# Revit family: Strangregulierventil für Differenzdruckmessung, Geradsitzform 4218 GMF
name_source: partatom
category: Rohrzubehör
units: mm (PartAtom-declared; Revit-internal decimal feet)

## family parameters
Arbeitsebenenbasiert = Nein
Beim Laden mit Abzugskörper schneiden = Nein
Bemaßung runder Anschluss = Durchmesser verwenden
Gemeinsam genutzt = Nein
Immer vertikal = Ja
OmniClass-Nummer = 23.65.55.14
OmniClass-Titel = Valves for Liquid Services
Teiletyp = Unterbricht

## types (1)
- Strangregulierventil für Differenzdruckmessung, Geradsitzform 4218 GMF
    Anwendungen = Zum hydraulischen Abgleich in Heiz- oder Kühlanlagen, Einregulieren und Absperren von Verteilleitungen, Strängen, Wärmetauschern, Heiz- und Kühlregistern.
    Ausführung = Geradsitzform, Gehäuse Grauguss GJL 250 nach EN 1561, Flansche nach EN 1092, PN 16; blau lackiert.
Messing Oberteil bis DN 100 geschraubt, ab DN 125 Ventiloberteil Grauguss mit nicht steigender Spindel, Spindelabdichtung durch Doppel-O-Ring.
Voreinstellung durch Hubbegrenzung mittels Innenspindel, digitale Anzeige der Voreinstellstufe im Handradfenster.
Zwei Schnellmessventile sind neben dem Handrad montiert.
    Differenzdruckmessnung = Das STRÖMAX-GMF Strangregulierventil ist mit zwei Schnellmessventilen ausgestattet:
Bei Verwendung eines geeigneten Messgerätes kann der Differenzdruck gemessen und dadurch die jeweilige Durchflussmenge in Abhängigkeit der Einstellstufe ermittelt werden.
An den HERZ-Messcomputern ist außerdem direkt die jeweilige Durchflussmenge ablesbar (siehe Gerätehandbuch).
    GT = 10 mm  [stored 0.0328084 ft]
    H07 = 10 mm  [stored 0.0328084 ft]
    Hersteller = HERZ Armaturen Ges.m.b.H.
    Max. Betriebsdruck = 1600000.0 Pa
    Max. Betriebstemperatur (ab DN40) = 110 °C
    Max. Betriebstemperatur (bis DN32) = 130 °C
    Medium = Heizwasserqualität entsprechend ÖNORM H 5195 bzw. VDI Richtlinie 2035.
Ethylen und Propylenglykol können in einem Verhältnis von 25-50 vol. [%] gemischt werden.
    O-Ringe = EPDM
    SCRNCODE = 05;07;02
    SCRNSEQ = ARM;ARM_TYP="STRV";2
    URL = www.herz-armaturen.at
    Ventilgehäuse = Grauguss GJL 250 nach EN 1561
    Ventiloberteil (ab DN125) = Grauguss
    Ventiloberteil (bis DN100) = Messing
    W02 = 60.00°

note: [stored X ft] marks values corroborated as IEEE doubles in the binary element streams (Revit-internal decimal feet)
